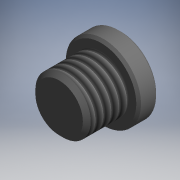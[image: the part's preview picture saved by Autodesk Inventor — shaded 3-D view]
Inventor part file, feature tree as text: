
AUTODESK INVENTOR PART (.ipt)
format: ipt  version: 2017.3 (Build 213256000, 256)  size: 120,832 bytes
history: native  units: mm (DEFAULTED — no unit token found)
features: other x7, sketch x2, revolve x1, thread x1, extrude x1
ambient origin geometry x8: Origin, YZ Plane, XZ Plane, XY Plane, X Axis, Y Axis, Z Axis, Center Point
bodies: Solid1 (feature_tree)
feature tree (12):
  revolve  "Revolution1"  [1 undecoded]
  thread  "Thread1"  [1 undecoded]
  extrude  "Extrusion1"  [1 undecoded]
  other  "din_908_XY"
  other  "din_908_YZ"
  other  "din_908_ZX"
  other  "din_908_X"
  other  "din_908_Y"
  other  "din_908_Z"
  other  "din_908_Center"
  sketch  "Sketch_1"  dims[d0=360.0deg d1=4.8mm d2=0.0mm d3=2.5mm d4=0.0mm]
  sketch  "Sketch_4"  dims[d5=0.0mm]
note: 3 required parameter values undecoded (feature->parameter linkage not recoverable at this tier; creation-order binding heuristic only, values carry confidence <= 0.55)